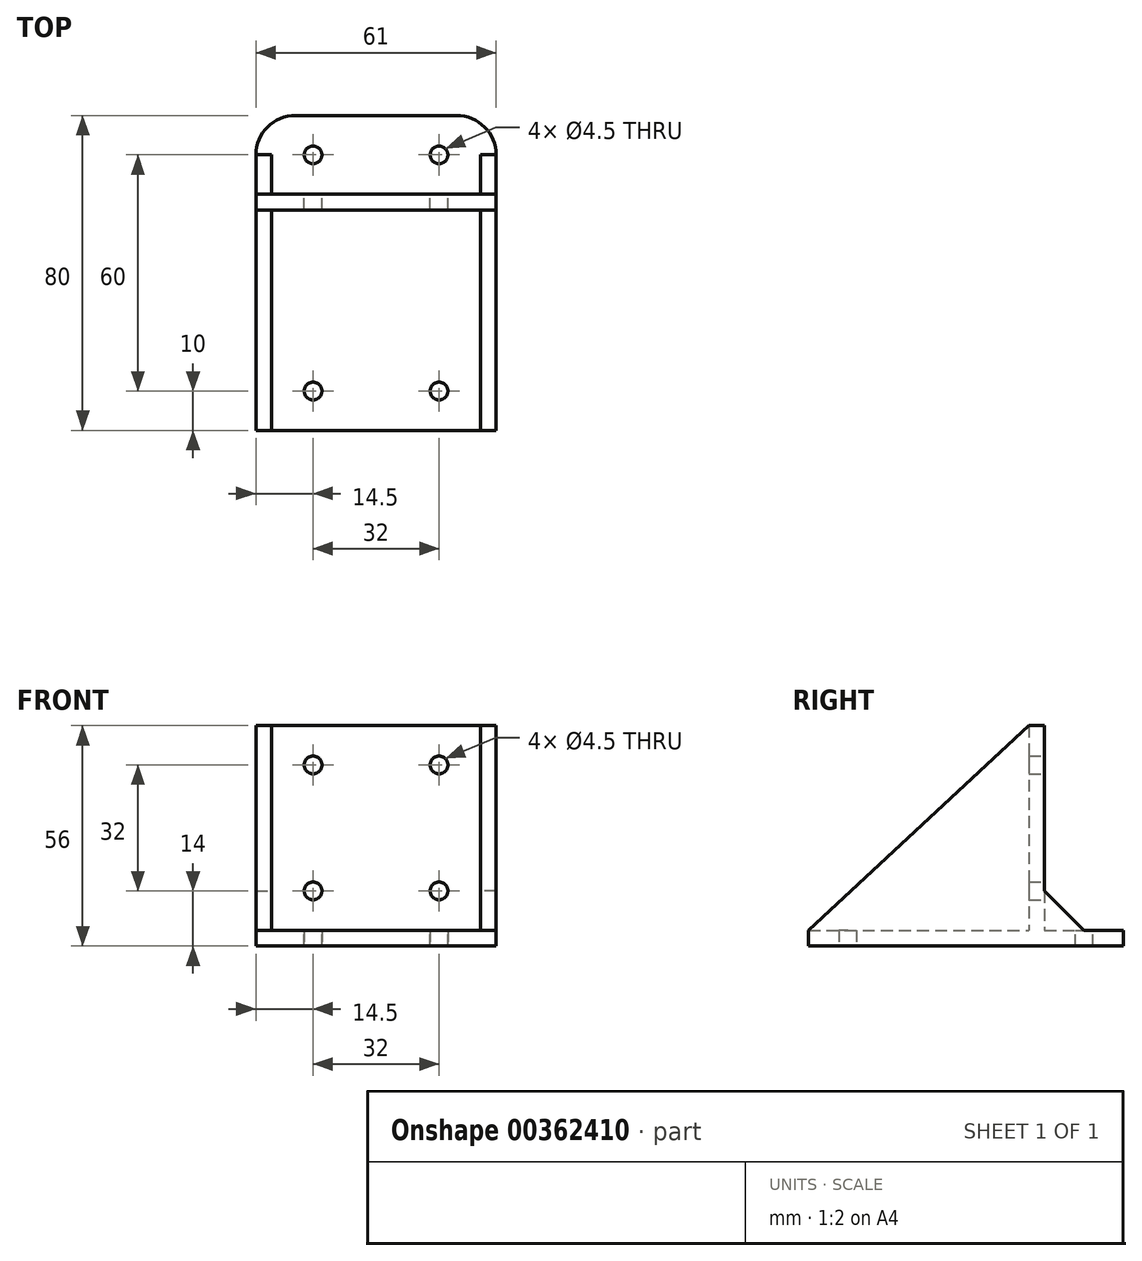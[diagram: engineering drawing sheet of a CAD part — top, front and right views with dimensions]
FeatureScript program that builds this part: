
annotation { "Feature Type Name" : "Feature", "Feature Type Description" : "" }
export const myFeature = defineFeature(function(context is Context, id is Id, definition is map)
    precondition{}
    {
        {
            var Q0;
            Q0=qCreatedBy(makeId("Top.planeOp"),FACE);
            var sketch = newSketch(context, id + "F0", { "sketchPlane" : qUnion([Q0])});
            skLineSegment(sketch, "E0.bottom", {"start": v(26.5, -30) * mm, "end": v(-26.5, -30) * mm});
            skLineSegment(sketch, "E0.top", {"start": v(26.5, 30) * mm, "end": v(-26.5, 30) * mm});
            skLineSegment(sketch, "E0.left", {"start": v(26.5, -30) * mm, "end": v(26.5, 30) * mm});
            skLineSegment(sketch, "E0.right", {"start": v(-26.5, -30) * mm, "end": v(-26.5, 30) * mm});
            skPoint(sketch, "E0.middle", {"position": v(0, 0) * mm});
            skSolve(sketch);
        }
        {
            var Q0;
            Q0=makeQuery(id+"F0.imprint","IMPRINT",FACE,{"disambiguationData":[TD([[makeQuery(id+"F0.imprint","IMPRINT",EDGE,{"derivedFrom":sQuery(id+"F0.wireOp",EDGE,"E0.bottom")}),-1.0]])]});
            extrude(context, id + "F1", {"entities" : qUnion([Q0]), "depth" : 4 * mm});
        }
        {
            var Q0;
            Q0=makeQuery(id+"F1.opExtrude","CAP_FACE",FACE,{"disambiguationData":[OSD([sQuery(id+"F0.wireOp",EDGE,"E0.bottom"),sQuery(id+"F0.wireOp",EDGE,"E0.top"),sQuery(id+"F0.wireOp",EDGE,"E0.left"),sQuery(id+"F0.wireOp",EDGE,"E0.right")])],"isStart":false});
            var sketch = newSketch(context, id + "F2", { "sketchPlane" : qUnion([Q0])});
            skLineSegment(sketch, "E1.bottom", {"start": v(-26.5, 30) * mm, "end": v(26.5, 30) * mm});
            skLineSegment(sketch, "E1.top", {"start": v(-26.5, 26) * mm, "end": v(26.5, 26) * mm});
            skLineSegment(sketch, "E1.left", {"start": v(-26.5, 30) * mm, "end": v(-26.5, 26) * mm});
            skLineSegment(sketch, "E1.right", {"start": v(26.5, 30) * mm, "end": v(26.5, 26) * mm});
            skSolve(sketch);
        }
        {
            var Q0;
            Q0=qSketchRegion(id+"F2",true);
            extrude(context, id + "F3", {"entities" : qUnion([Q0]), "operationType" : NewBodyOperationType.ADD, "depth" : 52 * mm});
        }
        {
            var Q0;
            Q0=makeQuery(id+"F1.opExtrude","CAP_FACE",FACE,{"disambiguationData":[OSD([sQuery(id+"F0.wireOp",EDGE,"E0.bottom"),sQuery(id+"F0.wireOp",EDGE,"E0.top"),sQuery(id+"F0.wireOp",EDGE,"E0.left"),sQuery(id+"F0.wireOp",EDGE,"E0.right")])],"isStart":true});
            var sketch = newSketch(context, id + "F4", { "sketchPlane" : qUnion([Q0])});
            skCircle(sketch, "E2", {"center": v(-16, 20) * mm, "radius": 2.25 * mm});
            skCircle(sketch, "E3.1.0.0", {"center": v(16, 20) * mm, "radius": 2.25 * mm});
            skLineSegment(sketch, "E3.direction1", {"start": v(-16, 20) * mm, "end": v(16, 20) * mm, "construction": true});
            skLineSegment(sketch, "E3.direction2", {"start": v(-16, 20) * mm, "end": v(-16, -20) * mm, "construction": true});
            skSolve(sketch);
        }
        {
            var Q0;
            Q0=makeQuery(id+"F4.imprint","IMPRINT",FACE,{"disambiguationData":[TD([[makeQuery(id+"F4.imprint","IMPRINT",EDGE,{"derivedFrom":sQuery(id+"F4.wireOp",EDGE,"E2")}),1.0]])]});
            var Q1;
            Q1=makeQuery(id+"F4.imprint","IMPRINT",FACE,{"disambiguationData":[TD([[makeQuery(id+"F4.imprint","IMPRINT",EDGE,{"derivedFrom":sQuery(id+"F4.wireOp",EDGE,"E3.1.0.0")}),1.0]])]});
            var Q2;
            Q2=makeQuery(id+"F4.imprint","IMPRINT",FACE,{"disambiguationData":[TD([[makeQuery(id+"F4.imprint","IMPRINT",EDGE,{"derivedFrom":sQuery(id+"F4.wireOp",EDGE,"E3.1.1.0")}),1.0]])]});
            var Q3;
            Q3=makeQuery(id+"F4.imprint","IMPRINT",FACE,{"disambiguationData":[TD([[makeQuery(id+"F4.imprint","IMPRINT",EDGE,{"derivedFrom":sQuery(id+"F4.wireOp",EDGE,"E3.0.1.0")}),1.0]])]});
            extrude(context, id + "F5", {"entities" : qUnion([Q0, Q1, Q2, Q3]), "operationType" : NewBodyOperationType.REMOVE, "endBound" : BoundingType.THROUGH_ALL, "oppositeDirection" : true, "depth" : 25 * mm});
        }
        {
            var Q0;
            Q0=makeQuery(id+"F3.boolean.opBoolean","MERGE",FACE,{"derivedFrom":[makeQuery(id+"F1.opExtrude","SWEPT_FACE",FACE,{"disambiguationData":[OSD([sQuery(id+"F0.wireOp",EDGE,"E0.top")])]}),makeQuery(id+"F3.opExtrude","SWEPT_FACE",FACE,{"disambiguationData":[OSD([sQuery(id+"F2.wireOp",EDGE,"E1.bottom")])]})]});
            var sketch = newSketch(context, id + "F6", { "sketchPlane" : qUnion([Q0])});
            skCircle(sketch, "E4.0.1.0", {"center": v(-16, 14) * mm, "radius": 2.25 * mm});
            skCircle(sketch, "E5.0.1.0", {"center": v(-16, 46) * mm, "radius": 2.25 * mm});
            skCircle(sketch, "E5.1.0.0", {"center": v(16, 14) * mm, "radius": 2.25 * mm});
            skCircle(sketch, "E5.1.1.0", {"center": v(16, 46) * mm, "radius": 2.25 * mm});
            skLineSegment(sketch, "E5.direction1", {"start": v(-16, 14) * mm, "end": v(16, 14) * mm, "construction": true});
            skLineSegment(sketch, "E5.direction2", {"start": v(-16, 14) * mm, "end": v(-16, 46) * mm, "construction": true});
            skSolve(sketch);
        }
        {
            var Q0;
            Q0=qSketchRegion(id+"F6",true);
            extrude(context, id + "F7", {"entities" : qUnion([Q0]), "operationType" : NewBodyOperationType.REMOVE, "endBound" : BoundingType.THROUGH_ALL, "oppositeDirection" : true, "depth" : 25 * mm});
        }
        {
            var Q0;
            Q0=makeQuery(id+"F3.boolean.opBoolean","MERGE",FACE,{"derivedFrom":[makeQuery(id+"F1.opExtrude","SWEPT_FACE",FACE,{"disambiguationData":[OSD([sQuery(id+"F0.wireOp",EDGE,"E0.left")])]}),makeQuery(id+"F3.opExtrude","SWEPT_FACE",FACE,{"disambiguationData":[OSD([sQuery(id+"F2.wireOp",EDGE,"E1.right")])]})]});
            var sketch = newSketch(context, id + "F8", { "sketchPlane" : qUnion([Q0])});
            skLineSegment(sketch, "E6", {"start": v(30, 56) * mm, "end": v(30, 0) * mm});
            skLineSegment(sketch, "E7", {"start": v(30, 0) * mm, "end": v(-30, 0) * mm});
            skLineSegment(sketch, "E8", {"start": v(-30, 0) * mm, "end": v(-30, 4) * mm});
            skLineSegment(sketch, "E9", {"start": v(-30, 4) * mm, "end": v(26, 56) * mm});
            skLineSegment(sketch, "E10", {"start": v(26, 56) * mm, "end": v(30, 56) * mm});
            skLineSegment(sketch, "E11", {"start": v(30, 4) * mm, "end": v(40, 4) * mm});
            skLineSegment(sketch, "E12", {"start": v(40, 4) * mm, "end": v(30, 14) * mm});
            skSolve(sketch);
        }
        {
            var Q0;
            Q0=qSketchRegion(id+"F8",true);
            extrude(context, id + "F9", {"entities" : qUnion([Q0]), "operationType" : NewBodyOperationType.ADD, "depth" : 4 * mm});
        }
        {
            var Q0;
            Q0=makeQuery(id+"F3.boolean.opBoolean","MERGE",FACE,{"derivedFrom":[makeQuery(id+"F1.opExtrude","SWEPT_FACE",FACE,{"disambiguationData":[OSD([sQuery(id+"F0.wireOp",EDGE,"E0.right")])]}),makeQuery(id+"F3.opExtrude","SWEPT_FACE",FACE,{"disambiguationData":[OSD([sQuery(id+"F2.wireOp",EDGE,"E1.left")])]})]});
            var sketch = newSketch(context, id + "F10", { "sketchPlane" : qUnion([Q0])});
            skLineSegment(sketch, "E13", {"start": v(-30, 56) * mm, "end": v(-26, 56) * mm});
            skLineSegment(sketch, "E14", {"start": v(-26, 56) * mm, "end": v(30, 4) * mm});
            skLineSegment(sketch, "E15", {"start": v(30, 4) * mm, "end": v(30, 0) * mm});
            skLineSegment(sketch, "E16", {"start": v(30, 0) * mm, "end": v(-30, 0) * mm});
            skLineSegment(sketch, "E17", {"start": v(-30, 0) * mm, "end": v(-30, 56) * mm});
            skLineSegment(sketch, "E18", {"start": v(-30, 4) * mm, "end": v(-40, 4) * mm});
            skLineSegment(sketch, "E19", {"start": v(-40, 4) * mm, "end": v(-30, 14) * mm});
            skLineSegment(sketch, "E20", {"start": v(-30, 14) * mm, "end": v(-30, 4) * mm});
            skSolve(sketch);
        }
        {
            var Q0;
            Q0=qSketchRegion(id+"F10",true);
            extrude(context, id + "F11", {"entities" : qUnion([Q0]), "operationType" : NewBodyOperationType.ADD, "depth" : 4 * mm});
        }
        {
            var Q0;
            Q0=makeQuery(id+"F11.boolean.opBoolean","MERGE",FACE,{"derivedFrom":[makeQuery(id+"F9.boolean.opBoolean","MERGE",FACE,{"derivedFrom":[makeQuery(id+"F3.boolean.opBoolean","MERGE",FACE,{"derivedFrom":[makeQuery(id+"F1.opExtrude","SWEPT_FACE",FACE,{"disambiguationData":[OSD([sQuery(id+"F0.wireOp",EDGE,"E0.top")])]}),makeQuery(id+"F3.opExtrude","SWEPT_FACE",FACE,{"disambiguationData":[OSD([sQuery(id+"F2.wireOp",EDGE,"E1.bottom")])]})]}),makeQuery(id+"F9.opExtrude","SWEPT_FACE",FACE,{"disambiguationData":[OSD([sQuery(id+"F8.wireOp",EDGE,"E6")])]})]}),makeQuery(id+"F11.opExtrude","SWEPT_FACE",FACE,{"disambiguationData":[OSD([sQuery(id+"F10.wireOp",EDGE,"E17")])]})]});
            var sketch = newSketch(context, id + "F12", { "sketchPlane" : qUnion([Q0])});
            skLineSegment(sketch, "E21.bottom", {"start": v(-30.5, 0) * mm, "end": v(30.5, 0) * mm});
            skLineSegment(sketch, "E21.top", {"start": v(-30.5, 4) * mm, "end": v(30.5, 4) * mm});
            skLineSegment(sketch, "E21.left", {"start": v(-30.5, 0) * mm, "end": v(-30.5, 4) * mm});
            skLineSegment(sketch, "E21.right", {"start": v(30.5, 0) * mm, "end": v(30.5, 4) * mm});
            skSolve(sketch);
        }
        {
            var Q0;
            Q0=qSketchRegion(id+"F12",true);
            extrude(context, id + "F13", {"entities" : qUnion([Q0]), "operationType" : NewBodyOperationType.ADD, "depth" : 20 * mm});
        }
        {
            var Q0;
            Q0=makeQuery(id+"F13.opExtrude","SWEPT_FACE",FACE,{"disambiguationData":[OSD([sQuery(id+"F12.wireOp",EDGE,"E21.top")])]});
            var sketch = newSketch(context, id + "F14", { "sketchPlane" : qUnion([Q0])});
            skCircle(sketch, "E22", {"center": v(-16, 40) * mm, "radius": 2.25 * mm});
            skCircle(sketch, "E23", {"center": v(16, 40) * mm, "radius": 2.25 * mm});
            skSolve(sketch);
        }
        {
            var Q0;
            Q0=makeQuery(id+"F14.imprint","IMPRINT",FACE,{"disambiguationData":[TD([[makeQuery(id+"F14.imprint","IMPRINT",EDGE,{"derivedFrom":sQuery(id+"F14.wireOp",EDGE,"E23")}),1.0]])]});
            var Q1;
            Q1=makeQuery(id+"F14.imprint","IMPRINT",FACE,{"disambiguationData":[TD([[makeQuery(id+"F14.imprint","IMPRINT",EDGE,{"derivedFrom":sQuery(id+"F14.wireOp",EDGE,"E22")}),1.0]])]});
            extrude(context, id + "F15", {"entities" : qUnion([Q0, Q1]), "operationType" : NewBodyOperationType.REMOVE, "endBound" : BoundingType.THROUGH_ALL, "oppositeDirection" : true, "depth" : 25 * mm});
        }
        {
            var Q0;
            Q0=makeQuery(id+"F13.opExtrude","CAP_EDGE",EDGE,{"disambiguationData":[OSD([sQuery(id+"F12.wireOp",EDGE,"E21.left")])],"isStart":false});
            var Q1;
            Q1=makeQuery(id+"F13.opExtrude","CAP_EDGE",EDGE,{"disambiguationData":[OSD([sQuery(id+"F12.wireOp",EDGE,"E21.right")])],"isStart":false});
            fillet(context, id + "F16", {"entities" : qUnion([Q0, Q1]), "radius" : 10 * mm, "tangentPropagation" : true, "allowEdgeOverflow" : false});
        }
    });
